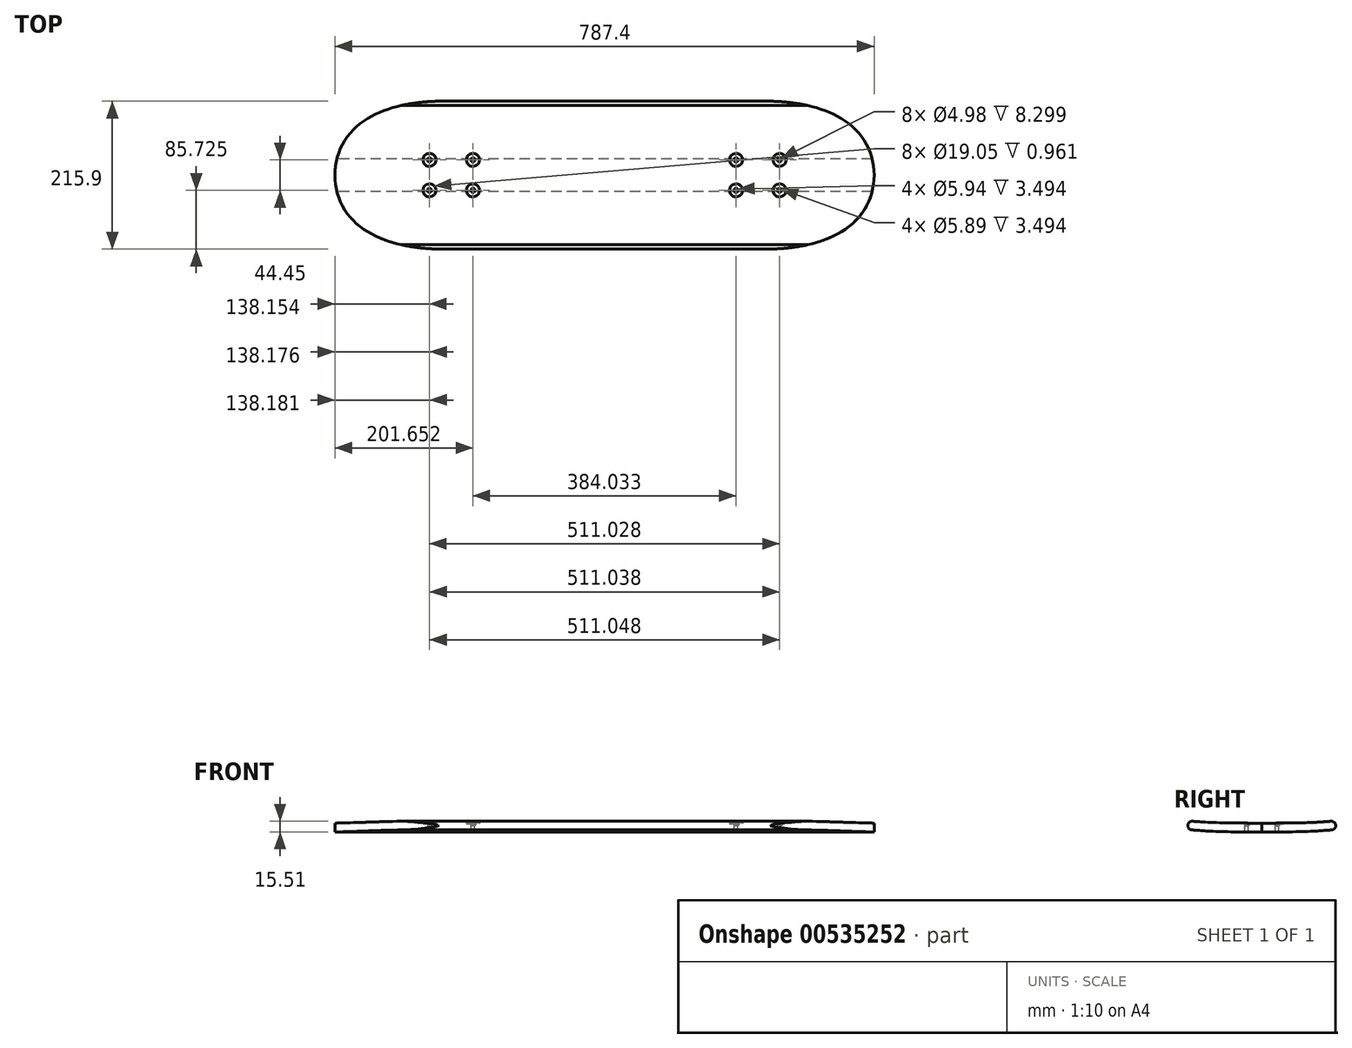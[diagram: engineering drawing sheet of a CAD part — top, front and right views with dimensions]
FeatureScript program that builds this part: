
annotation { "Feature Type Name" : "Feature", "Feature Type Description" : "" }
export const myFeature = defineFeature(function(context is Context, id is Id, definition is map)
    precondition{}
    {
        {
            var Q0;
            Q0=qCreatedBy(makeId("Right.planeOp"),FACE);
            var sketch = newSketch(context, id + "F0", { "sketchPlane" : qUnion([Q0])});
            skLineSegment(sketch, "E0.left", {"start": v(-107.95, 0) * mm, "end": v(-107.95, 0) * mm});
            skLineSegment(sketch, "E0.right", {"start": v(107.95, 0) * mm, "end": v(107.95, 0) * mm});
            skPoint(sketch, "E0.middle", {"position": v(0, 0) * mm});
            skPoint(sketch, "E1.visualSharp", {"position": v(107.95, 6.35) * mm});
            skArc(sketch, "E1.filletArc", {"start": v(107.95, 0) * mm, "mid": v(106.1, 4.5) * mm, "end": v(101.6, 6.35) * mm});
            skPoint(sketch, "E2.visualSharp", {"position": v(107.95, -6.35) * mm});
            skArc(sketch, "E2.filletArc", {"start": v(101.6, -6.35) * mm, "mid": v(106.1, -4.5) * mm, "end": v(107.95, 0) * mm});
            skPoint(sketch, "E3.visualSharp", {"position": v(-107.95, 6.35) * mm});
            skArc(sketch, "E3.filletArc", {"start": v(-101.6, 6.35) * mm, "mid": v(-106.1, 4.5) * mm, "end": v(-107.95, 0) * mm});
            skPoint(sketch, "E4.visualSharp", {"position": v(-107.95, -6.35) * mm});
            skArc(sketch, "E4.filletArc", {"start": v(-107.95, 0) * mm, "mid": v(-106.1, -4.5) * mm, "end": v(-101.6, -6.35) * mm});
            skPoint(sketch, "E5.center.orphan", {"position": v(0, 6.35) * mm});
            skPoint(sketch, "E6.center.orphan", {"position": v(0, -6.35) * mm});
            skLineSegment(sketch, "E7", {"start": v(0, 6.35) * mm, "end": v(0, -16.13) * mm, "construction": true});
            skFitSpline(sketch, "E8", {"points": [v(-101.6, 6.35) * mm, v(0, 3.56) * mm], "startDerivative": vector(99.66, -8.83) * mm, "endDerivative": vector(103.67, -0.32) * mm});
            skFitSpline(sketch, "E9", {"points": [v(-101.6, -6.35) * mm, v(0, -8.5) * mm], "startDerivative": vector(102.55, -8.8) * mm, "endDerivative": vector(103.62, 3.77) * mm});
            skFitSpline(sketch, "E10.MirrorCS", {"points": [v(101.6, -6.35) * mm, v(0, -8.5) * mm], "startDerivative": vector(-102.55, -8.8) * mm, "endDerivative": vector(-103.62, 3.77) * mm});
            skFitSpline(sketch, "E11.MirrorCS", {"points": [v(101.6, 6.35) * mm, v(0, 3.56) * mm], "startDerivative": vector(-99.66, -8.83) * mm, "endDerivative": vector(-103.67, -0.32) * mm});
            skPoint(sketch, "E12", {"position": v(23.79, -9.1) * mm});
            skLineSegment(sketch, "E13", {"start": v(23.79, -9.1) * mm, "end": v(-23.79, -9.1) * mm});
            skSolve(sketch);
        }
        {
            var Q0;
            Q0 = qSketchRegion(id + "F0", true);
            extrude(context, id + "F1", {"entities" : qUnion([Q0]), "depth" : 787.4 * mm, "offsetDistance" : 25.4 * mm});
        }
        {
            var Q0;
            Q0=qCreatedBy(makeId("Top.planeOp"),FACE);
            var sketch = newSketch(context, id + "F2", { "sketchPlane" : qUnion([Q0])});
            skFitSpline(sketch, "E14", {"points": [v(0, 0) * mm, v(161.12, 108.05) * mm], "startDerivative": vector(3.63, 195.57) * mm, "endDerivative": vector(317.3, 0.3) * mm});
            skFitSpline(sketch, "E15.MirrorCS", {"points": [v(0, 0) * mm, v(161.12, -108.05) * mm], "startDerivative": vector(3.63, -195.57) * mm, "endDerivative": vector(317.3, -0.3) * mm});
            skLineSegment(sketch, "E16", {"start": v(161.12, 108.05) * mm, "end": v(161.12, 193.44) * mm});
            skLineSegment(sketch, "E17", {"start": v(161.12, 193.44) * mm, "end": v(-168.91, 193.44) * mm});
            skLineSegment(sketch, "E18", {"start": v(-168.91, 193.44) * mm, "end": v(-168.91, -217.45) * mm});
            skLineSegment(sketch, "E19", {"start": v(-168.91, -217.45) * mm, "end": v(161.12, -217.45) * mm});
            skLineSegment(sketch, "E20", {"start": v(161.12, -217.45) * mm, "end": v(161.12, -108.05) * mm});
            skLineSegment(sketch, "E21", {"start": v(393.7, 170.34) * mm, "end": v(393.7, -200.48) * mm, "construction": true});
            skLineSegment(sketch, "E22.MirrorCS", {"start": v(626.28, -217.45) * mm, "end": v(626.28, -108.05) * mm});
            skLineSegment(sketch, "E23.MirrorCS", {"start": v(956.31, -217.45) * mm, "end": v(626.28, -217.45) * mm});
            skFitSpline(sketch, "E24.MirrorCS", {"points": [v(787.4, 0) * mm, v(626.28, -108.05) * mm], "startDerivative": vector(-3.63, -195.57) * mm, "endDerivative": vector(-317.3, -0.3) * mm});
            skLineSegment(sketch, "E25.MirrorCS", {"start": v(956.31, 193.44) * mm, "end": v(956.31, -217.45) * mm});
            skLineSegment(sketch, "E26.MirrorCS", {"start": v(626.28, 108.05) * mm, "end": v(626.28, 193.44) * mm});
            skLineSegment(sketch, "E27.MirrorCS", {"start": v(626.28, 193.44) * mm, "end": v(956.31, 193.44) * mm});
            skFitSpline(sketch, "E28.MirrorCS", {"points": [v(787.4, 0) * mm, v(626.28, 108.05) * mm], "startDerivative": vector(-3.63, 195.57) * mm, "endDerivative": vector(-317.3, 0.3) * mm});
            skPoint(sketch, "E29", {"position": v(156.94, 108.03) * mm});
            skPoint(sketch, "E30", {"position": v(155.78, 108.01) * mm});
            skSolve(sketch);
        }
        {
            var Q0;
            Q0=makeQuery(id+"F2.imprint","IMPRINT",FACE,{"disambiguationData":[TD([[makeQuery(id+"F2.imprint","IMPRINT",EDGE,{"derivedFrom":sQuery(id+"F2.wireOp",EDGE,"ab11eb16-b373-46bc-87d5-258dbd600a3c0.MirrorCS")}),1.0]])]});
            var Q1;
            Q1=makeQuery(id+"F2.imprint","IMPRINT",FACE,{"disambiguationData":[TD([[makeQuery(id+"F2.imprint","IMPRINT",EDGE,{"derivedFrom":sQuery(id+"F2.wireOp",EDGE,"E14")}),1.0]])]});
            var Q2;
            Q2=makeQuery(id+"F2.imprint","IMPRINT",FACE,{"disambiguationData":[TD([[makeQuery(id+"F2.imprint","IMPRINT",EDGE,{"derivedFrom":sQuery(id+"F2.wireOp",EDGE,"E22.MirrorCS")}),-1.0]])]});
            extrude(context, id + "F3", {"entities" : qUnion([Q0, Q1, Q2]), "operationType" : NewBodyOperationType.REMOVE, "oppositeDirection" : true, "depth" : 50.8 * mm, "offsetDistance" : 25.4 * mm, "hasSecondDirection" : true, "secondDirectionOppositeDirection" : false, "secondDirectionDepth" : 50.8 * mm});
        }
        {
            var Q0;
            Q0=qCreatedBy(makeId("Top.planeOp"),FACE);
            var sketch = newSketch(context, id + "F4", { "sketchPlane" : qUnion([Q0])});
            skCircle(sketch, "E31", {"center": v(138.18, -22.23) * mm, "radius": 2.49 * mm});
            skCircle(sketch, "E32", {"center": v(201.68, -22.23) * mm, "radius": 2.49 * mm});
            skCircle(sketch, "E33.MirrorC", {"center": v(138.18, 22.22) * mm, "radius": 2.49 * mm});
            skCircle(sketch, "E34.MirrorC", {"center": v(201.68, 22.22) * mm, "radius": 2.49 * mm});
            skLineSegment(sketch, "E35", {"start": v(393.7, 207.7) * mm, "end": v(393.7, -274.58) * mm, "construction": true});
            skCircle(sketch, "E36.MirrorC", {"center": v(585.72, 22.22) * mm, "radius": 2.49 * mm});
            skCircle(sketch, "E37.MirrorC", {"center": v(585.72, -22.23) * mm, "radius": 2.49 * mm});
            skCircle(sketch, "E38.MirrorC", {"center": v(649.22, -22.23) * mm, "radius": 2.49 * mm});
            skCircle(sketch, "E39.MirrorC", {"center": v(649.22, 22.22) * mm, "radius": 2.49 * mm});
            skSolve(sketch);
        }
        {
            var Q0;
            Q0 = qSketchRegion(id + "F4", true);
            extrude(context, id + "F5", {"entities" : qUnion([Q0]), "operationType" : NewBodyOperationType.REMOVE, "endBound" : BoundingType.THROUGH_ALL, "oppositeDirection" : true, "depth" : 50.8 * mm, "offsetDistance" : 25.4 * mm, "hasSecondDirection" : true, "secondDirectionBound" : SecondDirectionBoundingType.THROUGH_ALL, "secondDirectionOppositeDirection" : false, "secondDirectionDepth" : 127 * mm});
        }
        {
            var Q0;
            Q0=qCreatedBy(makeId("Top.planeOp"),FACE);
            var sketch = newSketch(context, id + "F6", { "sketchPlane" : qUnion([Q0])});
            skCircle(sketch, "E40", {"center": v(138.15, 22.23) * mm, "radius": 2.95 * mm});
            skLineSegment(sketch, "E41", {"start": v(393.67, 155.2) * mm, "end": v(393.67, -144.59) * mm, "construction": true});
            skCircle(sketch, "E42", {"center": v(201.65, 22.23) * mm, "radius": 2.97 * mm});
            skCircle(sketch, "E43.MirrorC", {"center": v(585.68, 22.23) * mm, "radius": 2.97 * mm});
            skCircle(sketch, "E44.MirrorC", {"center": v(649.18, 22.23) * mm, "radius": 2.95 * mm});
            skCircle(sketch, "E45.MirrorC", {"center": v(138.15, -22.23) * mm, "radius": 2.95 * mm});
            skCircle(sketch, "E46.MirrorC", {"center": v(201.65, -22.23) * mm, "radius": 2.97 * mm});
            skCircle(sketch, "E47.MirrorC", {"center": v(649.18, -22.23) * mm, "radius": 2.95 * mm});
            skCircle(sketch, "E48.MirrorC", {"center": v(585.68, -22.23) * mm, "radius": 2.97 * mm});
            skSolve(sketch);
        }
        {
            var Q0;
            Q0 = qSketchRegion(id + "F6", true);
            extrude(context, id + "F7", {"entities" : qUnion([Q0]), "operationType" : NewBodyOperationType.REMOVE, "depth" : 6.35 * mm, "offsetDistance" : 25.4 * mm, "hasSecondDirection" : true, "secondDirectionOppositeDirection" : true, "secondDirectionDepth" : 0.8 * mm});
        }
        {
            var Q0;
            Q0=qCreatedBy(makeId("Top.planeOp"),FACE);
            var sketch = newSketch(context, id + "F8", { "sketchPlane" : qUnion([Q0])});
            skCircle(sketch, "E49", {"center": v(138.18, 22.23) * mm, "radius": 9.53 * mm});
            skLineSegment(sketch, "E50", {"start": v(393.7, 155.75) * mm, "end": v(393.7, -148.32) * mm, "construction": true});
            skCircle(sketch, "E51", {"center": v(201.68, 22.23) * mm, "radius": 9.53 * mm});
            skCircle(sketch, "E52.MirrorC", {"center": v(201.68, -22.23) * mm, "radius": 9.53 * mm});
            skCircle(sketch, "E53.MirrorC", {"center": v(138.18, -22.23) * mm, "radius": 9.53 * mm});
            skCircle(sketch, "E54.MirrorC", {"center": v(585.72, -22.22) * mm, "radius": 9.53 * mm});
            skCircle(sketch, "E55.MirrorC", {"center": v(585.72, 22.23) * mm, "radius": 9.53 * mm});
            skCircle(sketch, "E56.MirrorC", {"center": v(649.22, 22.23) * mm, "radius": 9.53 * mm});
            skCircle(sketch, "E57.MirrorC", {"center": v(649.22, -22.22) * mm, "radius": 9.53 * mm});
            skSolve(sketch);
        }
        {
            var Q0;
            Q0 = qSketchRegion(id + "F8", true);
            extrude(context, id + "F9", {"entities" : qUnion([Q0]), "operationType" : NewBodyOperationType.REMOVE, "depth" : 3.67 * mm, "offsetDistance" : 25.4 * mm, "hasSecondDirection" : true, "secondDirectionOppositeDirection" : false, "secondDirectionDepth" : 2.7 * mm});
        }
    });
